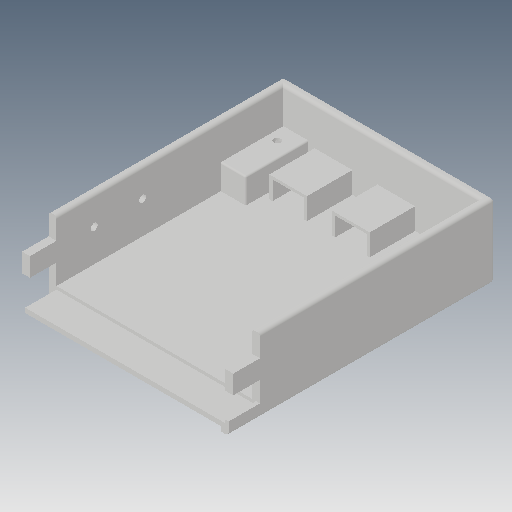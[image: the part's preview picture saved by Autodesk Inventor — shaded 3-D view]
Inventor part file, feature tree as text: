
AUTODESK INVENTOR PART (.ipt)
format: ipt  version: 2019 (Build 230136000, 136)  size: 412,160 bytes
history: native  units: mm
features: extrude x10, sketch x10, projected_geometry x5, other x5, fillet x2, plane x2, surface_op x1
ambient origin geometry x8: Origin, YZ Plane, XZ Plane, XY Plane, X Axis, Y Axis, Z Axis, Center Point
bodies: Solid1 (feature_tree)
feature tree (35):
  extrude  "Extrusion1"  Depth=170.0mm
  extrude  "Extrusion2"  Depth=5.0mm
  extrude  "Extrusion3"  Depth=25.0mm TaperAngle=0.0deg
  fillet  "Fillet1"  Radius=2.0mm
  extrude  "Extrusion4"  TaperAngle=0.0deg  [1 undecoded]
  extrude  "Extrusion5"  Depth=40.0mm
  fillet  "Fillet2"  [1 undecoded]
  plane  "Work Plane2"
  extrude  "Extrusion7"  Depth=35.0mm
  plane  "Work Plane1"
  extrude  "Extrusion8"  Depth=16.0mm TaperAngle=0.0deg
  surface_op  "Sculpt3"
  sketch  "Sketch8"  dims[d20=4.5mm d22=6.0mm]
  extrude  "Extrusion15"  Depth=6.0mm
  extrude  "Extrusion16"  Depth=7.0mm
  extrude  "Extrusion18"  Depth=1.0mm
  sketch  "Sketch1"  dims[d0=135.0mm d1=170.0mm]
  sketch  "Sketch2"  dims[d2=46.7mm d3=0.0mm d4=5.0mm]
  projected_geometry  "Projected Loop1"
  sketch  "Sketch3"  dims[d5=38.7mm d6=0.0mm d7=25.0mm d8=0.0mm d9=2.0mm]
  projected_geometry  "Projected Loop2"
  sketch  "Sketch4"  dims[d10=0.0mm d11=0.0mm]
  sketch  "Sketch5"  dims[d12=16.0mm d13=40.0mm d14=0.0mm]
  sketch  "Sketch6"  dims[d15=0.0mm d16=35.0mm]
  sketch  "Sketch7"  dims[d17=16.0mm d18=16.0mm d19=0.0mm]
  sketch  "Sketch14"  dims[d23=4.5mm d24=7.0mm]
  projected_geometry  "Projected Loop10"
  sketch  "Sketch16"  dims[d26=12.0mm d27=0.0mm d28=1.0mm d29=4.5mm d30=4.5mm d31=30.8mm d34=90.0mm d37=0.0mm d38=0.0mm d39=-1.5mm d40=7.5mm d41=7.5mm d42=3.15mm d43=0.0mm d44=10.0mm d45=12.5mm d46=18.0mm d51=20.0mm d70=1.75mm d91=12.0mm d92=8.0mm d93=2.05mm d94=2.05mm d95=20.0mm d96=29.0mm d97=0.0mm d98=0.8mm d99=0.8mm d100=1.8mm d101=4.4mm d102=0.0mm d105=1.8mm d106=4.4mm d107=0.0mm]
  projected_geometry  "Projected Loop13"
  projected_geometry  "Projected Loop14"
  other  "Composite3"
  other  "Srf3"
  parser-record x1  (decoder bookkeeping rows leaked as tree rows — omitted from the tree; the rows remain in map.json)
  other  "Case B.iam"
  other  "Case_B1:1"
note: 2 required parameter values undecoded (feature->parameter linkage not recoverable at this tier; creation-order binding heuristic only, values carry confidence <= 0.55)
note: 1 file-system path scrubbed to <path> (originals preserved in map.json)
